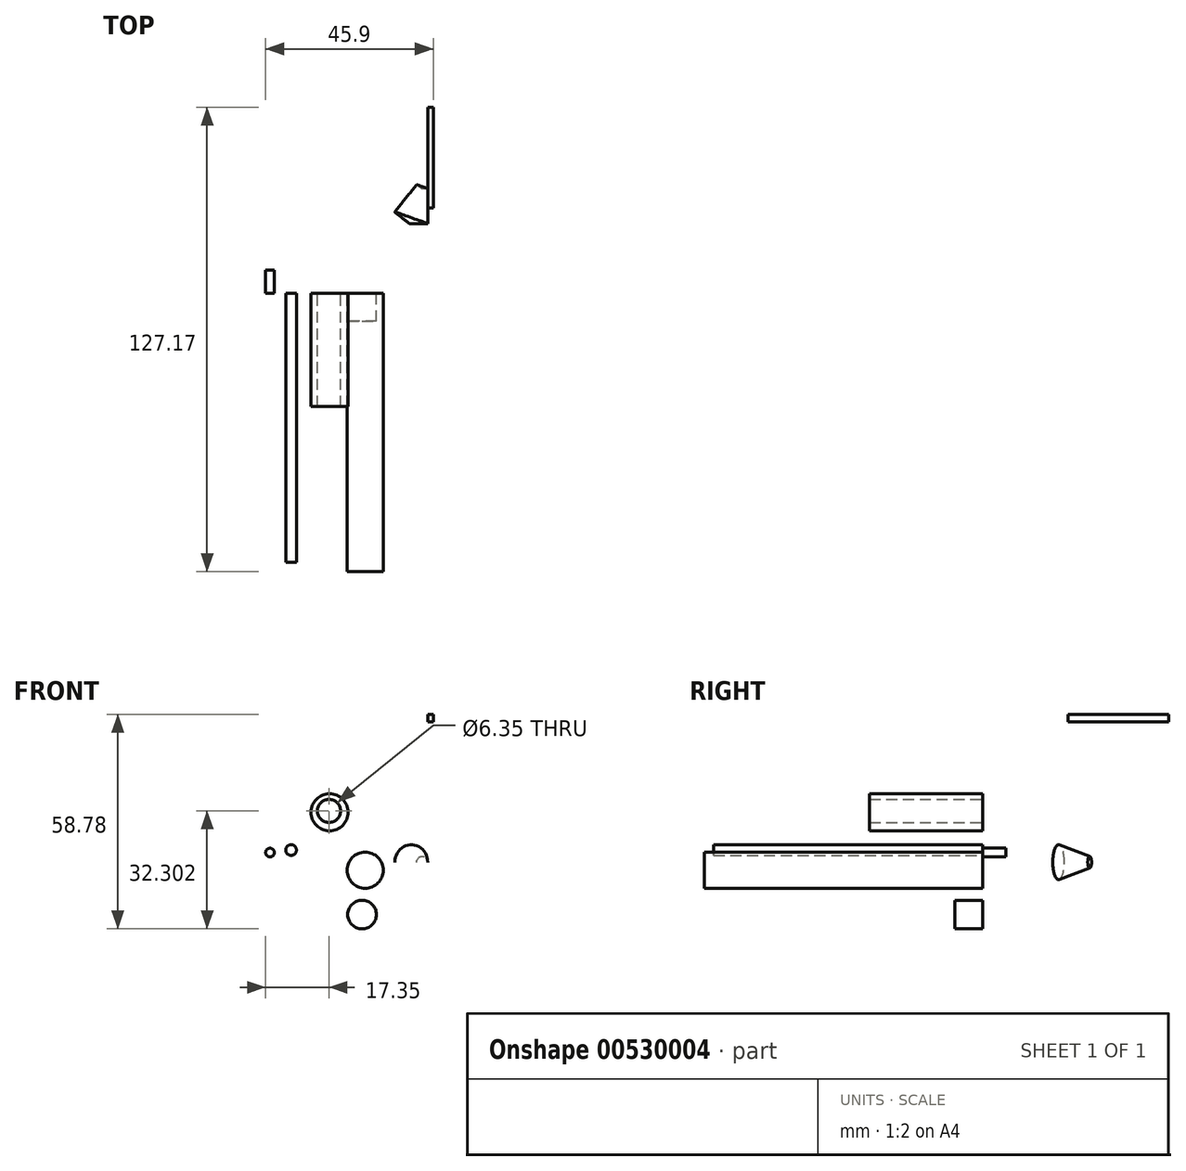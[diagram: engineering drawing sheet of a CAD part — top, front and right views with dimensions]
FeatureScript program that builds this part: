
annotation { "Feature Type Name" : "Feature", "Feature Type Description" : "" }
export const myFeature = defineFeature(function(context is Context, id is Id, definition is map)
    precondition{}
    {
        {
            var Q0;
            Q0=qCreatedBy(makeId("Top.planeOp"),FACE);
            var sketch = newSketch(context, id + "F0", { "sketchPlane" : qUnion([Q0])});
            skLineSegment(sketch, "E0", {"start": v(0, 28.75) * mm, "end": v(-1.7, 28.75) * mm});
            skLineSegment(sketch, "E1", {"start": v(-1.7, 28.75) * mm, "end": v(-5.08, 19.17) * mm});
            skLineSegment(sketch, "E2", {"start": v(0, 19.17) * mm, "end": v(-5.08, 19.17) * mm});
            skLineSegment(sketch, "E3", {"start": v(0, 19.17) * mm, "end": v(0, 28.75) * mm});
            skSolve(sketch);
        }
        {
            var Q0;
            Q0=makeQuery(id+"F0.imprint","IMPRINT",FACE,{"disambiguationData":[TD([[makeQuery(id+"F0.imprint","IMPRINT",EDGE,{"derivedFrom":sQuery(id+"F0.wireOp",EDGE,"E0")}),1.0]])]});
            var Q1;
            Q1=sQuery(id+"F0.wireOp",EDGE,"E1");
            revolve(context, id + "F1", {"entities" : qUnion([Q0]), "axis" : qUnion([Q1]), "revolveType" : RevolveType.FULL});
        }
        {
            var Q0;
            Q0=qCreatedBy(makeId("Front.planeOp"),FACE);
            var sketch = newSketch(context, id + "F2", { "sketchPlane" : qUnion([Q0])});
            skCircle(sketch, "E4", {"center": v(-17.13, -2.2) * mm, "radius": 4.96 * mm});
            skSolve(sketch);
        }
        {
            var Q0;
            Q0=makeQuery(id+"F2.imprint","IMPRINT",FACE,{"disambiguationData":[TD([[makeQuery(id+"F2.imprint","IMPRINT",EDGE,{"derivedFrom":sQuery(id+"F2.wireOp",EDGE,"E4")}),1.0]])]});
            extrude(context, id + "F3", {"entities" : qUnion([Q0]), "depth" : 76.2 * mm, "offsetDistance" : 25.4 * mm});
        }
        {
            var Q0;
            Q0=qCreatedBy(makeId("Front.planeOp"),FACE);
            var sketch = newSketch(context, id + "F4", { "sketchPlane" : qUnion([Q0])});
            skCircle(sketch, "E5", {"center": v(-17.97, -14.33) * mm, "radius": 3.92 * mm});
            skSolve(sketch);
        }
        {
            var Q0;
            Q0=makeQuery(id+"F4.imprint","IMPRINT",FACE,{"disambiguationData":[TD([[makeQuery(id+"F4.imprint","IMPRINT",EDGE,{"derivedFrom":sQuery(id+"F4.wireOp",EDGE,"E5")}),1.0]])]});
            extrude(context, id + "F5", {"entities" : qUnion([Q0]), "depth" : 7.62 * mm, "offsetDistance" : 25.4 * mm});
        }
        {
            var Q0;
            Q0=qCreatedBy(makeId("Front.planeOp"),FACE);
            var sketch = newSketch(context, id + "F6", { "sketchPlane" : qUnion([Q0])});
            skCircle(sketch, "E6", {"center": v(-43.18, 2.64) * mm, "radius": 1.2 * mm});
            skSolve(sketch);
        }
        {
            var Q0;
            Q0=makeQuery(id+"F6.imprint","IMPRINT",FACE,{"disambiguationData":[TD([[makeQuery(id+"F6.imprint","IMPRINT",EDGE,{"derivedFrom":sQuery(id+"F6.wireOp",EDGE,"E6")}),1.0]])]});
            extrude(context, id + "F7", {"entities" : qUnion([Q0]), "oppositeDirection" : true, "depth" : 6.35 * mm, "offsetDistance" : 25.4 * mm});
        }
        {
            var Q0;
            Q0=qCreatedBy(makeId("Right.planeOp"),FACE);
            var sketch = newSketch(context, id + "F8", { "sketchPlane" : qUnion([Q0])});
            skLineSegment(sketch, "E7.bottom", {"start": v(23.42, 40.52) * mm, "end": v(50.97, 40.52) * mm});
            skLineSegment(sketch, "E7.top", {"start": v(23.42, 38.46) * mm, "end": v(50.97, 38.46) * mm});
            skLineSegment(sketch, "E7.left", {"start": v(23.42, 40.52) * mm, "end": v(23.42, 38.46) * mm});
            skLineSegment(sketch, "E7.right", {"start": v(50.97, 40.52) * mm, "end": v(50.97, 38.46) * mm});
            skSolve(sketch);
        }
        {
            var Q0;
            Q0=makeQuery(id+"F8.imprint","IMPRINT",FACE,{"disambiguationData":[TD([[makeQuery(id+"F8.imprint","IMPRINT",EDGE,{"derivedFrom":sQuery(id+"F8.wireOp",EDGE,"E7.bottom")}),-1.0]])]});
            extrude(context, id + "F9", {"entities" : qUnion([Q0]), "depth" : 1.52 * mm, "offsetDistance" : 25.4 * mm});
        }
        {
            var Q0;
            Q0=qCreatedBy(makeId("Front.planeOp"),FACE);
            var sketch = newSketch(context, id + "F10", { "sketchPlane" : qUnion([Q0])});
            skCircle(sketch, "E8", {"center": v(-26.86, 13.66) * mm, "radius": 5.08 * mm});
            skSolve(sketch);
        }
        {
            var Q0;
            Q0=makeQuery(id+"F10.imprint","IMPRINT",FACE,{"disambiguationData":[TD([[makeQuery(id+"F10.imprint","IMPRINT",EDGE,{"derivedFrom":sQuery(id+"F10.wireOp",EDGE,"E8")}),1.0]])]});
            extrude(context, id + "F11", {"entities" : qUnion([Q0]), "depth" : 30.99 * mm, "offsetDistance" : 25.4 * mm});
        }
        {
            var Q0;
            Q0=qCreatedBy(makeId("Front.planeOp"),FACE);
            var sketch = newSketch(context, id + "F12", { "sketchPlane" : qUnion([Q0])});
            skPoint(sketch, "E9", {"position": v(-27.03, 14.04) * mm});
            skSolve(sketch);
        }
        {
            var Q0;
            Q0=sQuery(id+"F12.wireOp",VERTEX,"E9");
            var Q1;
            Q1=makeQuery(id+"F11.opExtrude","SWEPT_BODY",BODY,{"disambiguationData":[OSD([sQuery(id+"F10.wireOp",EDGE,"E8")])]});
            hole(context, id + "F13", {"style" : HoleStyle.SIMPLE, "endStyle" : HoleEndStyle.THROUGH, "oppositeDirection" : true, "holeDiameter" : 6.35 * mm, "isTappedThrough" : true, "tappedDepth" : 12.7 * mm, "tapClearance" : 3, "locations" : qUnion([Q0]), "scope" : qUnion([Q1])});
        }
        {
            var Q0;
            Q0=qCreatedBy(makeId("Right.planeOp"),FACE);
            var sketch = newSketch(context, id + "F14", { "sketchPlane" : qUnion([Q0])});
            skCircle(sketch, "E10", {"center": v(24.9, -16.23) * mm, "radius": 4.21 * mm});
            skSolve(sketch);
        }
        {
            var Q0;
            Q0=sQuery(id+"F14.wireOp",EDGE,"E10");
            extrude(context, id + "F15", {"bodyType" : ToolBodyType.SURFACE, "surfaceEntities" : qUnion([Q0]), "oppositeDirection" : true, "depth" : 0.25 * mm, "offsetDistance" : 25.4 * mm});
        }
        {
            var Q0;
            Q0=qCreatedBy(makeId("Front.planeOp"),FACE);
            var sketch = newSketch(context, id + "F16", { "sketchPlane" : qUnion([Q0])});
            skCircle(sketch, "E11", {"center": v(-37.42, 3.33) * mm, "radius": 1.47 * mm});
            skSolve(sketch);
        }
        {
            var Q0;
            Q0=makeQuery(id+"F16.imprint","IMPRINT",FACE,{"disambiguationData":[TD([[makeQuery(id+"F16.imprint","IMPRINT",EDGE,{"derivedFrom":sQuery(id+"F16.wireOp",EDGE,"E11")}),1.0]])]});
            extrude(context, id + "F17", {"entities" : qUnion([Q0]), "depth" : 73.66 * mm, "offsetDistance" : 25.4 * mm});
        }
    });
